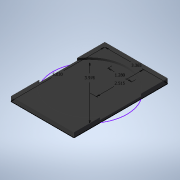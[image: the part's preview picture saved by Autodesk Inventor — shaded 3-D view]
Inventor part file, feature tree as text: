
AUTODESK INVENTOR PART (.ipt)
format: ipt  version: 2020 (Build 240168000, 168)  size: 116,224 bytes
history: native  units: in
note: dims shown in document units (in); Inventor stores cm internally (conversion verified against a paired STEP export)
features: extrude x2, sketch x1
ambient origin geometry x8: Origin, YZ Plane, XZ Plane, XY Plane, X Axis, Y Axis, Z Axis, Center Point
bodies: Solid1 (feature_tree)
feature tree (3):
  sketch  "Sketch1"  dims[d0=3.3654in d1=5.0299in d2=2.515in d3=3.9764in d4=1.2795in d5=0.25in d6=0.0in d7=0.125in d8=0.0in]
  extrude  "Extrusion1"  Depth=5.0299in
  extrude  "Extrusion2"  Depth=0.125in
